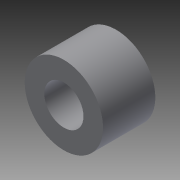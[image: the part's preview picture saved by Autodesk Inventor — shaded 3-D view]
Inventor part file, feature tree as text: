
AUTODESK INVENTOR PART (.ipt)
format: ipt  version: 2014 (Build 180170000, 170)  size: 83,456 bytes
history: native  units: mm
features: extrude x1, plane x1, sketch x1
ambient origin geometry x8: Origin, YZ Plane, XZ Plane, XY Plane, X Axis, Y Axis, Z Axis, Center Point
bodies: Solid1 (feature_tree)
feature tree (3):
  extrude  "Extrusion1"  Depth=4.0mm
  plane  "Work Plane1"
  sketch  "Sketch1"  dims[d0=3.0mm d1=6.0mm d2=4.0mm d3=0.0mm]
